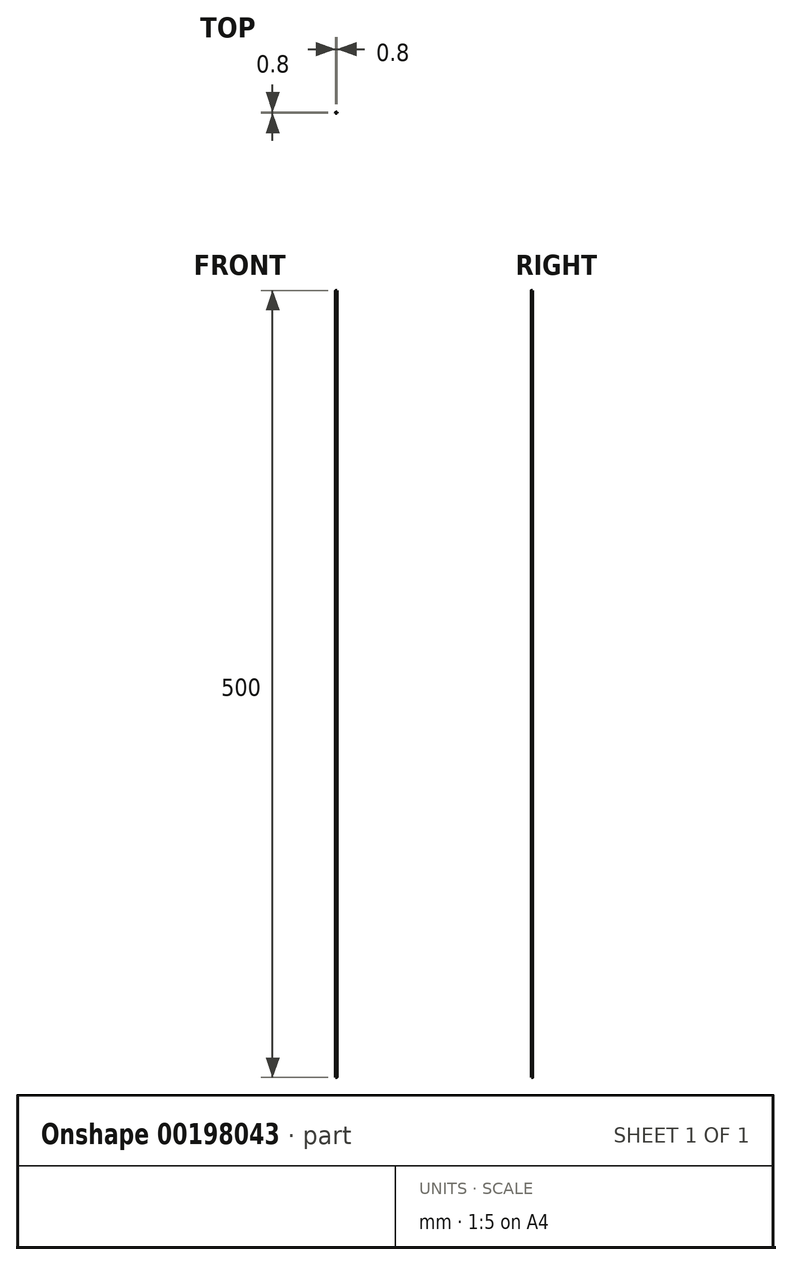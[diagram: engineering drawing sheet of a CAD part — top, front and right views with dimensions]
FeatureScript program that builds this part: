
annotation { "Feature Type Name" : "Feature", "Feature Type Description" : "" }
export const myFeature = defineFeature(function(context is Context, id is Id, definition is map)
    precondition{}
    {
        {
            var Q0;
            Q0=qCreatedBy(makeId("Right.planeOp"),FACE);
            var sketch = newSketch(context, id + "F0", { "sketchPlane" : qUnion([Q0])});
            skLineSegment(sketch, "E0", {"start": v(0, 0) * mm, "end": v(0, 500) * mm});
            skSolve(sketch);
        }
        {
            var Q0;
            Q0=qCreatedBy(makeId("Top.planeOp"),FACE);
            var sketch = newSketch(context, id + "F1", { "sketchPlane" : qUnion([Q0])});
            skCircle(sketch, "E1", {"center": v(0, 0) * mm, "radius": 0.4 * mm});
            skSolve(sketch);
        }
        {
            var Q0;
            Q0=makeQuery(id+"F1.imprint","IMPRINT",FACE,{"disambiguationData":[TD([[makeQuery(id+"F1.imprint","IMPRINT",EDGE,{"derivedFrom":sQuery(id+"F1.wireOp",EDGE,"E1")}),1.0]])]});
            var Q1;
            Q1=sQuery(id+"F0.wireOp",EDGE,"E0");
            sweep(context, id + "F2", {"profiles" : qUnion([Q0]), "path" : qUnion([Q1])});
        }
    });
